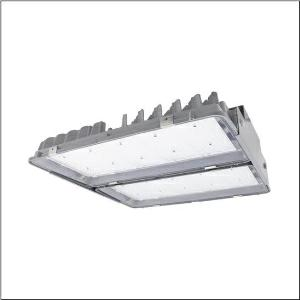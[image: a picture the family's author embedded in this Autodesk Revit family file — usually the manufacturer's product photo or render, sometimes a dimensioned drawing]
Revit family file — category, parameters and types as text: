
# Revit family: highbay_11xtreme_51hf61db4tma
name_source: partatom
category: Lighting Fixtures
units: mm (PartAtom-declared; Revit-internal decimal feet)

## family parameters
Cut with Voids When Loaded = No
Host = Face
Light Source = No
Part Type = Normal
Room Calculation Point = No
Round Connector Dimension = Use Diameter
Shared = No

## types (1)
- --- (1 x LED, 54000 lm, 282.6 W, 4000K)
    Apparent Load = 283 VA
    CIE Flux Codes = 88 96 99 100 100
    Color Rendering = 80
    Color Temperature = 4000K
    Default Elevation = 1800 mm
    Description = Highbay 11Xtreme, LED high bay luminaire, primary light control with lens, of PMMA, primary optical cover: cover, of toughened safety glass, light emission: direct distribution, primary light characteristic: symmetric, installation type: suspended mounting, surface-mounted, 2x LED module,for 1x 2x LED, rated luminous flux: 54.000lm, luminous efficacy: 191lm/W, light colour: 840, colour temperature: 4000K, with cable H07RN-F 5x 1.5mm², mains connection: 220..240V, AC, 50/60Hz, cable length: 1,5m, rated input power: 283W, luminaire housing, of diecast aluminium, coated, silver, length: 595mm, width: 560mm, height: 195mm, protection rating (complete): IP66, insulation class (complete): insulation class I (protective earthing), certification: CE, ENEC, UKCA, protection symbol: D, ball protection: ball impact resistant according to DIN VDE 0710 part 13 (with chain suspension), impact resistance: IK08, permissible operating ambient temperature: -25..+60°C, reducing of maximum allowable ambient temperature of 5°C with ceiling mounting, packaging unit: 1 piece
    Height = 157 mm
    Lamp = 1 x LED
    Lamp Light Flux = 54000 lm
    Lamp Power = 282.6 W
    Lamp count = 1
    Length = 593 mm
    Luminous efficacy = 191 lm/W
    Manufacturer = Siteco
    ModVariant = No
    Model = 51HF61DB4TMA
    Mounting Place = Ceiling
    Mounting Type = Pendant
    Number of Poles = 1
    OnlyDefault = Yes
    Power Factor = 1
    Product Name = Highbay 11Xtreme
    Product group = LED high bay luminaire
    ProductGroupID = 903
    Protection Class = Protection class I
    Protection Degree = IP 66
    RLX_Detail_Level = 1
    RLX_Emergency_Light_Flux = 0 lm
    RLX_Emergency_Type = 0
    RLX_Emergency_Type_DB = No
    RlxData = <blob elided: 33817 chars, md5=fcd65d92>
    Socket = socket
    Standby Power = 0 W
    System Light Flux = 53999 lm
    System Power = 283 W
    Type Comments = factory setting: luminous flux: 100 % | dim-lin: 254 | 960 mA
    Type Image = l_1258340.jpg
    URL = http://relux.com
    VarID = @adj_052851
    Voltage = 0 V
    Weight = 0.00 kg
    Width = 278 mm

## geometry (parser evidence)
native form markers: Blend x4, Sweep x11
no freeform markers — native parametric forms only
